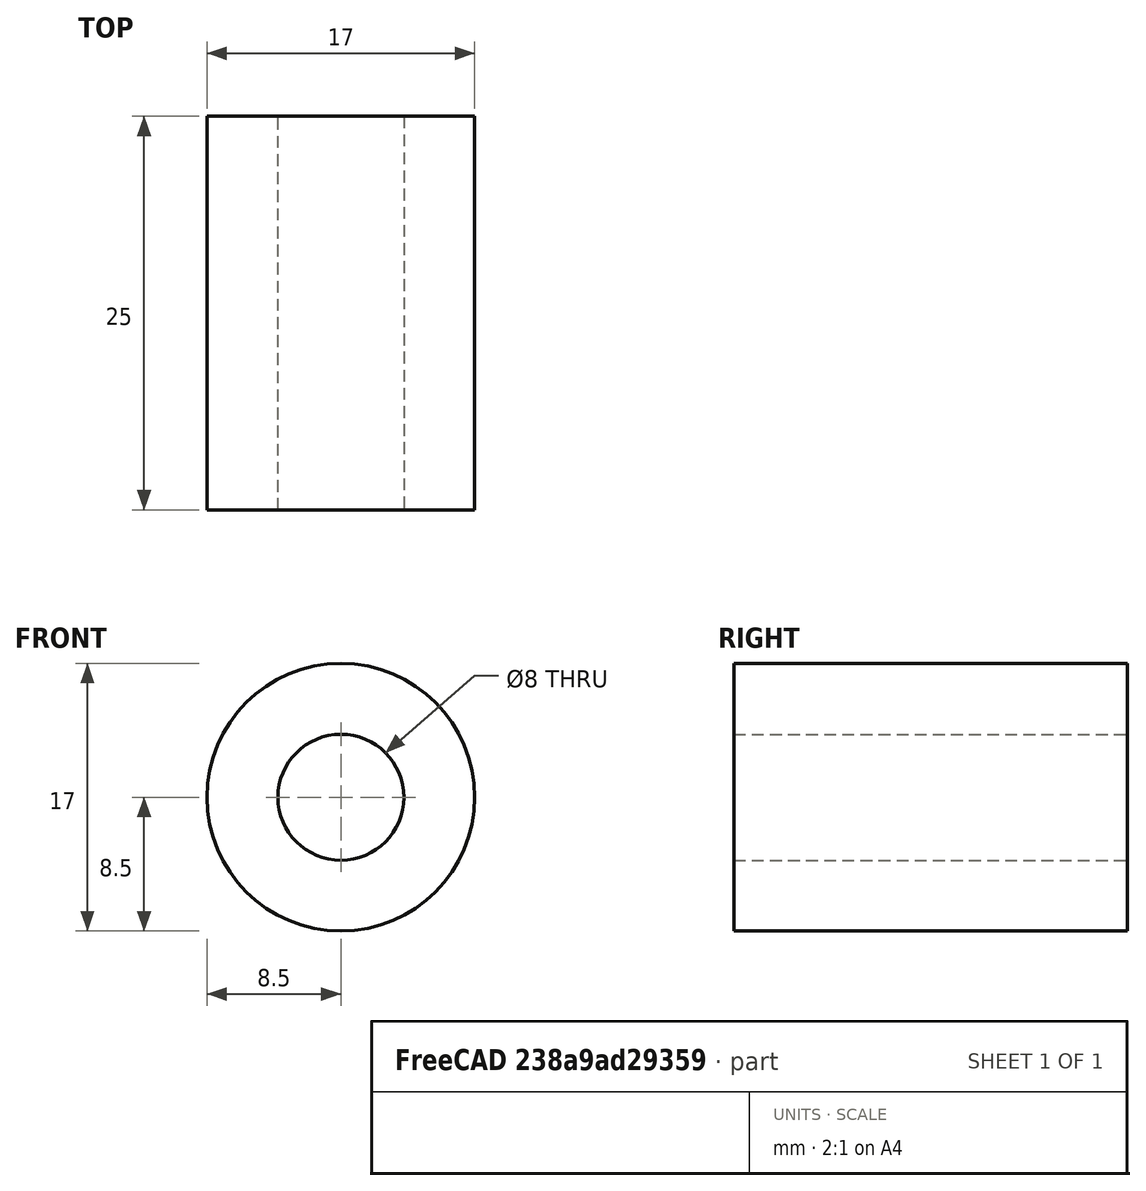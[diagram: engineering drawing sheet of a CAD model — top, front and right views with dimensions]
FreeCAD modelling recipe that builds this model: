
FCSTD DOCUMENT  (FreeCAD 0.18R4 (GitTag))
Label: cople
License: All rights reserved
LicenseURL: http://en.wikipedia.org/wiki/All_rights_reserved
objects: Sketcher::SketchObject×1, PartDesign::Pad×1, PartDesign::Body×1
note: 4 computed .brp shape members not serialized (recipe doc carries the construction recipe); baked Part::Feature solids carry a one-line shape summary decoded from their .brp

FEATURE [Sketcher::SketchObject] Sketch
  MapMode = 5
  Placement = pos=(0,0,0) rot=(1,0,0;1.5708rad)
  Support = -> [XZ_Plane]
  sketch-geometry (2):
    g0: Circle CenterX=0 CenterY=0 CenterZ=0 NormalX=0 NormalY=0 NormalZ=1 AngleXU=0 Radius=8.5
    g1: Circle CenterX=0 CenterY=0 CenterZ=0 NormalX=0 NormalY=0 NormalZ=1 AngleXU=0 Radius=4
  constraints (2):
    c: Radius(g0) = 8.5
    c: Radius(g1) = 4
FEATURE [PartDesign::Pad] Pad
  Length = 25
  Length2 = 100
  Placement = pos=(0,0,0) rot=(1,0,0;1.5708rad)
  Profile = -> Sketch
  Type = 0
FEATURE [PartDesign::Body] Body
  Group = -> [Sketch,Pad]
  Origin = -> Origin
  Tip = -> Pad
